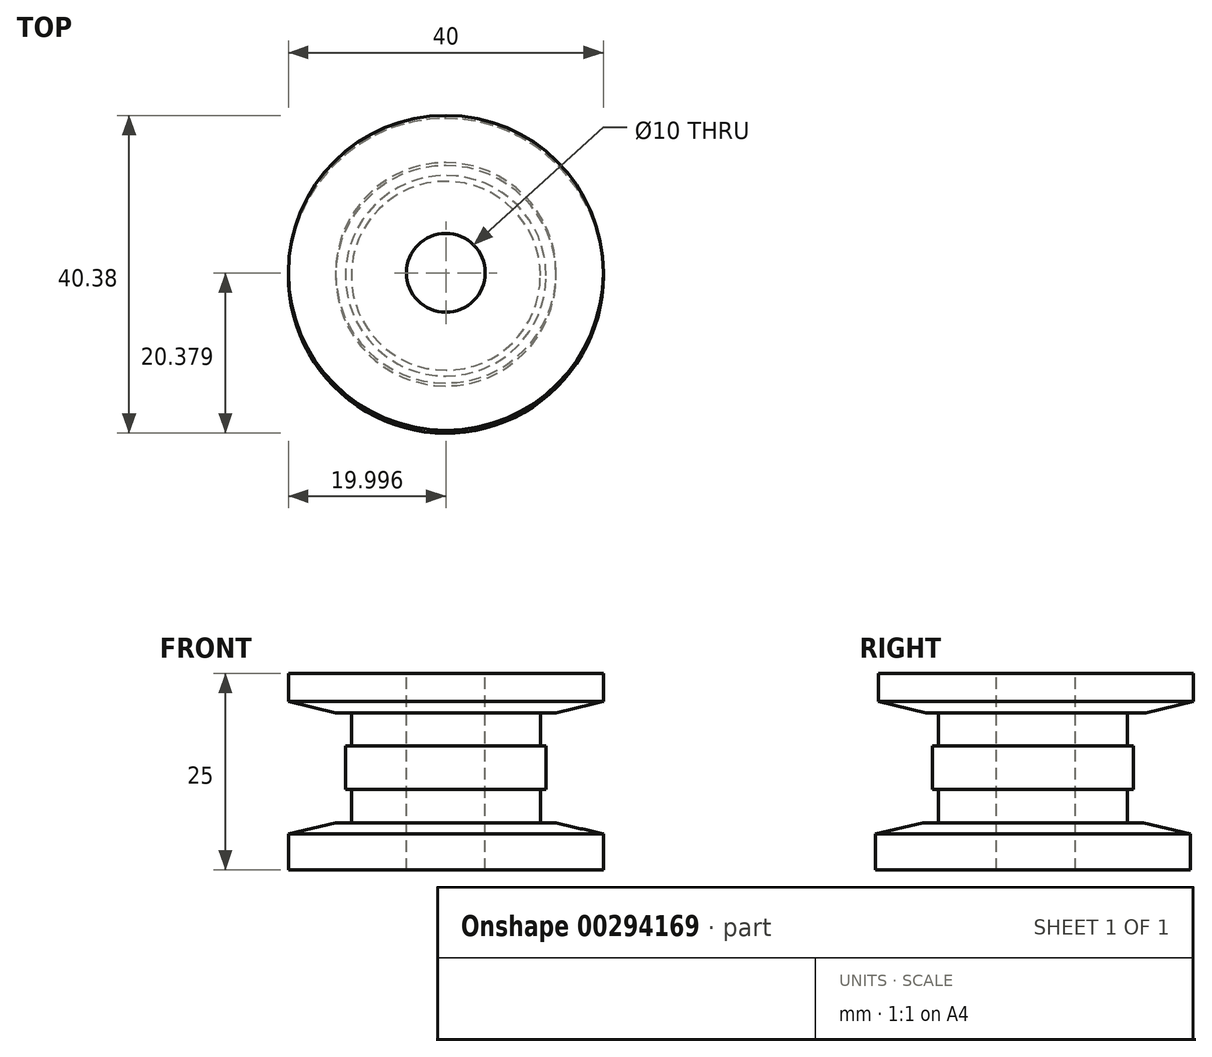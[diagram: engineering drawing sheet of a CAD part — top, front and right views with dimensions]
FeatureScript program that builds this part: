
annotation { "Feature Type Name" : "Feature", "Feature Type Description" : "" }
export const myFeature = defineFeature(function(context is Context, id is Id, definition is map)
    precondition{}
    {
        {
            var Q0;
            Q0=qCreatedBy(makeId("Top.planeOp"),FACE);
            var sketch = newSketch(context, id + "F0", { "sketchPlane" : qUnion([Q0])});
            skCircle(sketch, "E0", {"center": v(-4.7, 29.07) * mm, "radius": 20 * mm});
            skSolve(sketch);
        }
        {
            var Q0;
            Q0=makeQuery(id+"F0.imprint","IMPRINT",FACE,{"disambiguationData":[TD([[makeQuery(id+"F0.imprint","IMPRINT",EDGE,{"derivedFrom":sQuery(id+"F0.wireOp",EDGE,"E0")}),1.0]])]});
            extrude(context, id + "F1", {"entities" : qUnion([Q0]), "depth" : 6 * mm});
        }
        {
            var Q0;
            Q0=makeQuery(id+"F1.opExtrude","CAP_FACE",FACE,{"disambiguationData":[OSD([sQuery(id+"F0.wireOp",EDGE,"E0")])],"isStart":false});
            var sketch = newSketch(context, id + "F2", { "sketchPlane" : qUnion([Q0])});
            skCircle(sketch, "E1", {"center": v(-4.7, 29.07) * mm, "radius": 12 * mm});
            skSolve(sketch);
        }
        {
            var Q0;
            Q0=makeQuery(id+"F2.imprint","IMPRINT",FACE,{"disambiguationData":[TD([[makeQuery(id+"F2.imprint","IMPRINT",EDGE,{"derivedFrom":sQuery(id+"F2.wireOp",EDGE,"E1")}),1.0]])]});
            extrude(context, id + "F3", {"entities" : qUnion([Q0]), "operationType" : NewBodyOperationType.ADD, "depth" : 4.25 * mm});
        }
        {
            var Q0;
            Q0=makeQuery(id+"F3.opExtrude","CAP_FACE",FACE,{"disambiguationData":[OSD([sQuery(id+"F2.wireOp",EDGE,"E1")])],"isStart":false});
            var sketch = newSketch(context, id + "F4", { "sketchPlane" : qUnion([Q0])});
            skCircle(sketch, "E2", {"center": v(-4.7, 29.07) * mm, "radius": 12.75 * mm});
            skSolve(sketch);
        }
        {
            var Q0;
            Q0 = qSketchRegion(id + "F4", true);
            extrude(context, id + "F5", {"entities" : qUnion([Q0]), "operationType" : NewBodyOperationType.ADD, "depth" : 5.5 * mm});
        }
        {
            var Q0;
            Q0=makeQuery(id+"F5.opExtrude","CAP_FACE",FACE,{"disambiguationData":[OSD([sQuery(id+"F4.wireOp",EDGE,"E2")])],"isStart":false});
            var sketch = newSketch(context, id + "F6", { "sketchPlane" : qUnion([Q0])});
            skCircle(sketch, "E3", {"center": v(-4.7, 29.07) * mm, "radius": 12 * mm});
            skSolve(sketch);
        }
        {
            var Q0;
            Q0=makeQuery(id+"F6.imprint","IMPRINT",FACE,{"disambiguationData":[TD([[makeQuery(id+"F6.imprint","IMPRINT",EDGE,{"derivedFrom":sQuery(id+"F6.wireOp",EDGE,"E3")}),1.0]])]});
            var sketch = newSketch(context, id + "F7", { "sketchPlane" : qUnion([Q0])});
            skSolve(sketch);
        }
        {
            var Q0;
            Q0 = qSketchRegion(id + "F7", true);
            var Q1;
            Q1=makeQuery(id+"F6.imprint","IMPRINT",FACE,{"disambiguationData":[TD([[makeQuery(id+"F6.imprint","IMPRINT",EDGE,{"derivedFrom":sQuery(id+"F6.wireOp",EDGE,"E3")}),1.0]])]});
            extrude(context, id + "F8", {"entities" : qUnion([Q0, Q1]), "operationType" : NewBodyOperationType.ADD, "depth" : 4.25 * mm});
        }
        {
            var Q0;
            Q0=makeQuery(id+"F8.opExtrude","CAP_FACE",FACE,{"disambiguationData":[OSD([sQuery(id+"F6.wireOp",EDGE,"E3")])],"isStart":false});
            var sketch = newSketch(context, id + "F9", { "sketchPlane" : qUnion([Q0])});
            skCircle(sketch, "E4", {"center": v(-4.7, 29.07) * mm, "radius": 20 * mm});
            skSolve(sketch);
        }
        {
            var Q0;
            Q0=makeQuery(id+"F9.imprint","IMPRINT",FACE,{"disambiguationData":[TD([[makeQuery(id+"F9.imprint","IMPRINT",EDGE,{"derivedFrom":makeQuery(id+"F8.opExtrude","CAP_EDGE",EDGE,{"disambiguationData":[OSD([sQuery(id+"F6.wireOp",EDGE,"E3")])],"isStart":false})}),1.0]])]});
            var sketch = newSketch(context, id + "F10", { "sketchPlane" : qUnion([Q0])});
            skCircle(sketch, "E5", {"center": v(-4.7, 29.45) * mm, "radius": 20 * mm});
            skSolve(sketch);
        }
        {
            var Q0;
            Q0 = qSketchRegion(id + "F10", true);
            extrude(context, id + "F11", {"entities" : qUnion([Q0]), "operationType" : NewBodyOperationType.ADD, "depth" : 5 * mm});
        }
        {
            var Q0;
            Q0=makeQuery(id+"F11.opExtrude","CAP_FACE",FACE,{"disambiguationData":[OSD([sQuery(id+"F10.wireOp",EDGE,"E5")])],"isStart":false});
            var sketch = newSketch(context, id + "F12", { "sketchPlane" : qUnion([Q0])});
            skCircle(sketch, "E6", {"center": v(-4.7, 29.45) * mm, "radius": 5 * mm});
            skSolve(sketch);
        }
        {
            var Q0;
            Q0 = qSketchRegion(id + "F12", true);
            extrude(context, id + "F13", {"entities" : qUnion([Q0]), "operationType" : NewBodyOperationType.REMOVE, "endBound" : BoundingType.THROUGH_ALL, "oppositeDirection" : true, "depth" : 25 * mm});
        }
        {
            var Q0;
            Q0=makeQuery(id+"F1.opExtrude","CAP_EDGE",EDGE,{"disambiguationData":[OSD([sQuery(id+"F0.wireOp",EDGE,"E0")])],"isStart":false});
            chamfer(context, id + "F14", {"entities" : qUnion([Q0]), "chamferType" : ChamferType.TWO_OFFSETS, "width1" : 6 * mm, "oppositeDirection" : false, "width2" : 1.4 * mm, "tangentPropagation" : true});
        }
        {
            var Q0;
            Q0=makeQuery(id+"F11.opExtrude","CAP_EDGE",EDGE,{"disambiguationData":[OSD([sQuery(id+"F10.wireOp",EDGE,"E5")])],"isStart":true});
            chamfer(context, id + "F15", {"entities" : qUnion([Q0]), "chamferType" : ChamferType.TWO_OFFSETS, "width1" : 1.4 * mm, "oppositeDirection" : false, "width2" : 6 * mm, "tangentPropagation" : true});
        }
    });
